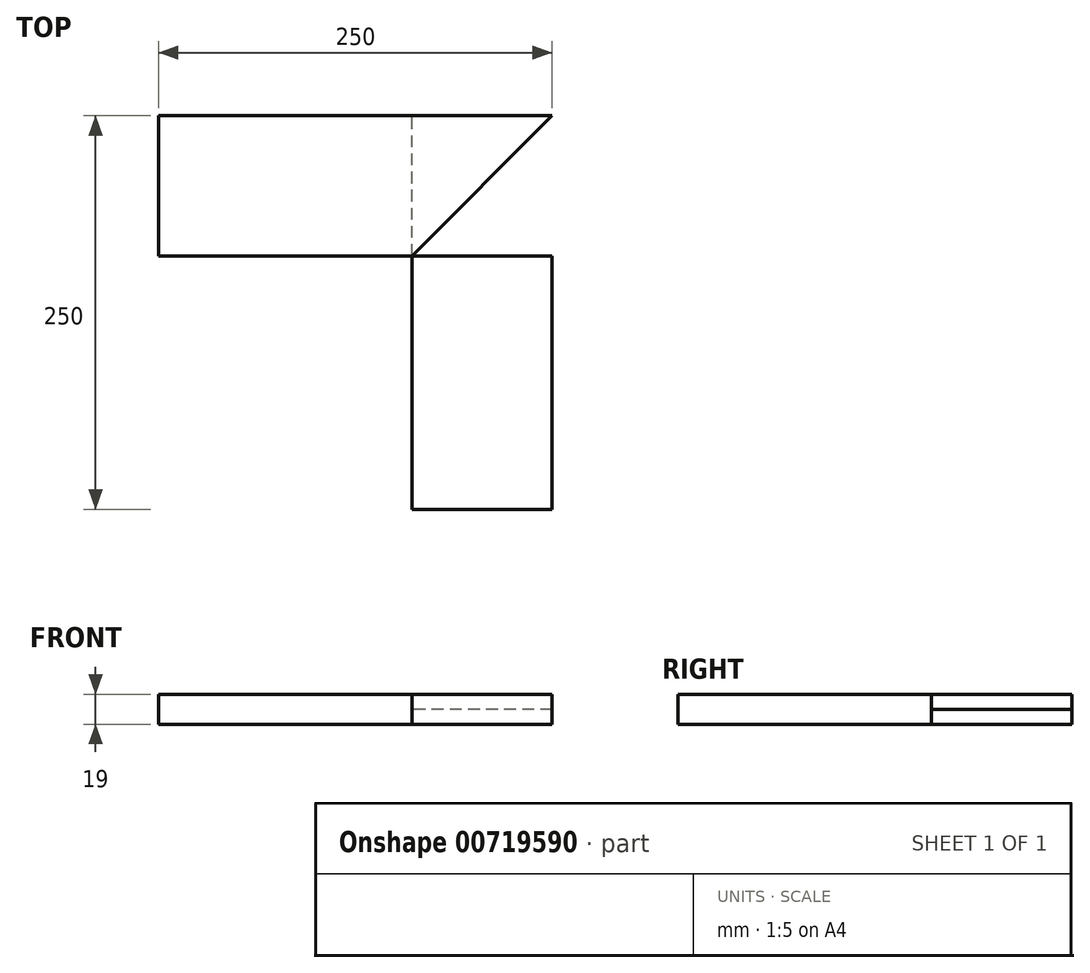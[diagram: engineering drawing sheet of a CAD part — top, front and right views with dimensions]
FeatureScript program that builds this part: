
annotation { "Feature Type Name" : "Feature", "Feature Type Description" : "" }
export const myFeature = defineFeature(function(context is Context, id is Id, definition is map)
    precondition{}
    {
        {
            var Q0;
            Q0=qCreatedBy(makeId("Top.planeOp"),FACE);
            var sketch = newSketch(context, id + "F0", { "sketchPlane" : qUnion([Q0])});
            skLineSegment(sketch, "E0.bottom", {"start": v(0, 0) * mm, "end": v(-250, 0) * mm});
            skLineSegment(sketch, "E0.top", {"start": v(0, -89) * mm, "end": v(-250, -89) * mm});
            skLineSegment(sketch, "E0.left", {"start": v(0, 0) * mm, "end": v(0, -89) * mm});
            skLineSegment(sketch, "E0.right", {"start": v(-250, 0) * mm, "end": v(-250, -89) * mm});
            skSolve(sketch);
        }
        {
            var Q0;
            Q0=makeQuery(id+"F0.imprint","IMPRINT",FACE,{"disambiguationData":[TD([[makeQuery(id+"F0.imprint","IMPRINT",EDGE,{"derivedFrom":sQuery(id+"F0.wireOp",EDGE,"E0.bottom")}),1.0]])]});
            extrude(context, id + "F1", {"entities" : qUnion([Q0]), "depth" : 19 * mm, "offsetDistance" : 25 * mm});
        }
        {
            var Q0;
            Q0=qCreatedBy(makeId("Top.planeOp"),FACE);
            var sketch = newSketch(context, id + "F2", { "sketchPlane" : qUnion([Q0])});
            skLineSegment(sketch, "E1.bottom", {"start": v(0, 0) * mm, "end": v(-89, 0) * mm});
            skLineSegment(sketch, "E1.top", {"start": v(0, -250) * mm, "end": v(-89, -250) * mm});
            skLineSegment(sketch, "E1.left", {"start": v(0, 0) * mm, "end": v(0, -250) * mm});
            skLineSegment(sketch, "E1.right", {"start": v(-89, 0) * mm, "end": v(-89, -250) * mm});
            skSolve(sketch);
        }
        {
            var Q0;
            Q0=makeQuery(id+"F2.imprint","IMPRINT",FACE,{"disambiguationData":[TD([[makeQuery(id+"F2.imprint","IMPRINT",EDGE,{"derivedFrom":sQuery(id+"F2.wireOp",EDGE,"E1.bottom")}),1.0]])]});
            extrude(context, id + "F3", {"entities" : qUnion([Q0]), "depth" : 19 * mm, "offsetDistance" : 25 * mm});
        }
        {
            var Q0;
            Q0=makeQuery(id+"F1.opExtrude","CAP_FACE",FACE,{"disambiguationData":[OSD([sQuery(id+"F0.wireOp",EDGE,"E0.bottom"),sQuery(id+"F0.wireOp",EDGE,"E0.top"),sQuery(id+"F0.wireOp",EDGE,"E0.left"),sQuery(id+"F0.wireOp",EDGE,"E0.right")])],"isStart":false});
            var sketch = newSketch(context, id + "F4", { "sketchPlane" : qUnion([Q0])});
            skLineSegment(sketch, "E2", {"start": v(0, 0) * mm, "end": v(-89, -89) * mm});
            skSolve(sketch);
        }
        {
            var Q0;
            {var subQ0=sQuery(id+"F4.wireOp",EDGE,"E2");Q0=makeQuery(id+"F4.imprint","IMPRINT",FACE,{"disambiguationData":[TD([[makeQuery(id+"F4.imprint","IMPRINT",EDGE,{"derivedFrom":subQ0}),1.0]])]});}
            extrude(context, id + "F5", {"entities" : qUnion([Q0]), "operationType" : NewBodyOperationType.REMOVE, "endBound" : BoundingType.THROUGH_ALL, "oppositeDirection" : true, "depth" : 25 * mm, "offsetDistance" : 25 * mm});
        }
        {
            var Q0;
            Q0=makeQuery(id+"F1.opExtrude","CAP_FACE",FACE,{"disambiguationData":[OSD([sQuery(id+"F0.wireOp",EDGE,"E0.bottom"),sQuery(id+"F0.wireOp",EDGE,"E0.top"),sQuery(id+"F0.wireOp",EDGE,"E0.left"),sQuery(id+"F0.wireOp",EDGE,"E0.right")])],"isStart":true});
            var sketch = newSketch(context, id + "F6", { "sketchPlane" : qUnion([Q0])});
            skLineSegment(sketch, "E3", {"start": v(-89, 89) * mm, "end": v(-89, 0) * mm});
            skSolve(sketch);
        }
        {
            var Q0;
            {var subQ0=sQuery(id+"F6.wireOp",EDGE,"E3");Q0=makeQuery(id+"F6.imprint","IMPRINT",FACE,{"disambiguationData":[TD([[makeQuery(id+"F6.imprint","IMPRINT",EDGE,{"derivedFrom":subQ0}),1.0]])]});}
            extrude(context, id + "F7", {"entities" : qUnion([Q0]), "operationType" : NewBodyOperationType.REMOVE, "oppositeDirection" : true, "depth" : (19 / 2) * mm, "offsetDistance" : 25 * mm});
        }
        {
            var Q0;
            Q0=makeQuery(id+"F1.opExtrude","SWEPT_BODY",BODY,{"disambiguationData":[OSD([sQuery(id+"F0.wireOp",EDGE,"E0.bottom"),sQuery(id+"F0.wireOp",EDGE,"E0.top"),sQuery(id+"F0.wireOp",EDGE,"E0.left"),sQuery(id+"F0.wireOp",EDGE,"E0.right")])]});
            var Q1;
            Q1=makeQuery(id+"F3.opExtrude","SWEPT_BODY",BODY,{"disambiguationData":[OSD([sQuery(id+"F2.wireOp",EDGE,"E1.bottom"),sQuery(id+"F2.wireOp",EDGE,"E1.top"),sQuery(id+"F2.wireOp",EDGE,"E1.left"),sQuery(id+"F2.wireOp",EDGE,"E1.right")])]});
            booleanBodies(context, id + "F8", {"operationType" : BooleanOperationType.SUBTRACTION, "tools" : qUnion([Q0]), "targets" : qUnion([Q1]), "keepTools" : true});
        }
    });
